# Revit family: CU2W
name_source: partatom
category: Lighting Fixtures
units: mm (PartAtom-declared; Revit-internal decimal feet)

## family parameters
Cut with Voids When Loaded = No
Host = Face
Light Source = No
OmniClass Number = 23.80.70.11.11
OmniClass Title = General Luminaries, Non Directional
Part Type = Normal
Room Calculation Point = No
Round Connector Dimension = Use Diameter
Shared = No

## types (1)
- CU2W
    Apparent Load = 3 VA
    Body = Paint -  Matte White
    Certification = UL924 Damp Listed, NFPA 101 and NFPA 70
    Default Elevation = 48 "
    Description = Emergency lighting fixture combining LED performance and value with a compact and attractive wet location LED based emergency light.
    Features = LED life-cycle of more than 10 years
•	 Quick installation
•	 Dual-voltage 120 or 277V AC input
•	 Includes long-life 9.6VDC Nickel Cadmium battery
for UL recognized 90 minute operation
•	 Remote capacity or extended runtime option
•	 Wet Location Listed (0°C to 50°C)
•	 Fully adjustable lamp-heads
•	 Provided with water-proof test switch and
AC-On indicator
    Glass = Glass - White
    Lamp = LED
    Manufacturer = Compass Products
    Model = CU2W
    Steel = Metal-Galvanized_Steel
    Type Comments = Light Fixture
    URL = https://www.currentlighting.com
    Warranty = 2 year full unit warranty
    Wattage Comments = 2.7W

## geometry (parser evidence)
native form markers: Sweep x5
no freeform markers — native parametric forms only
